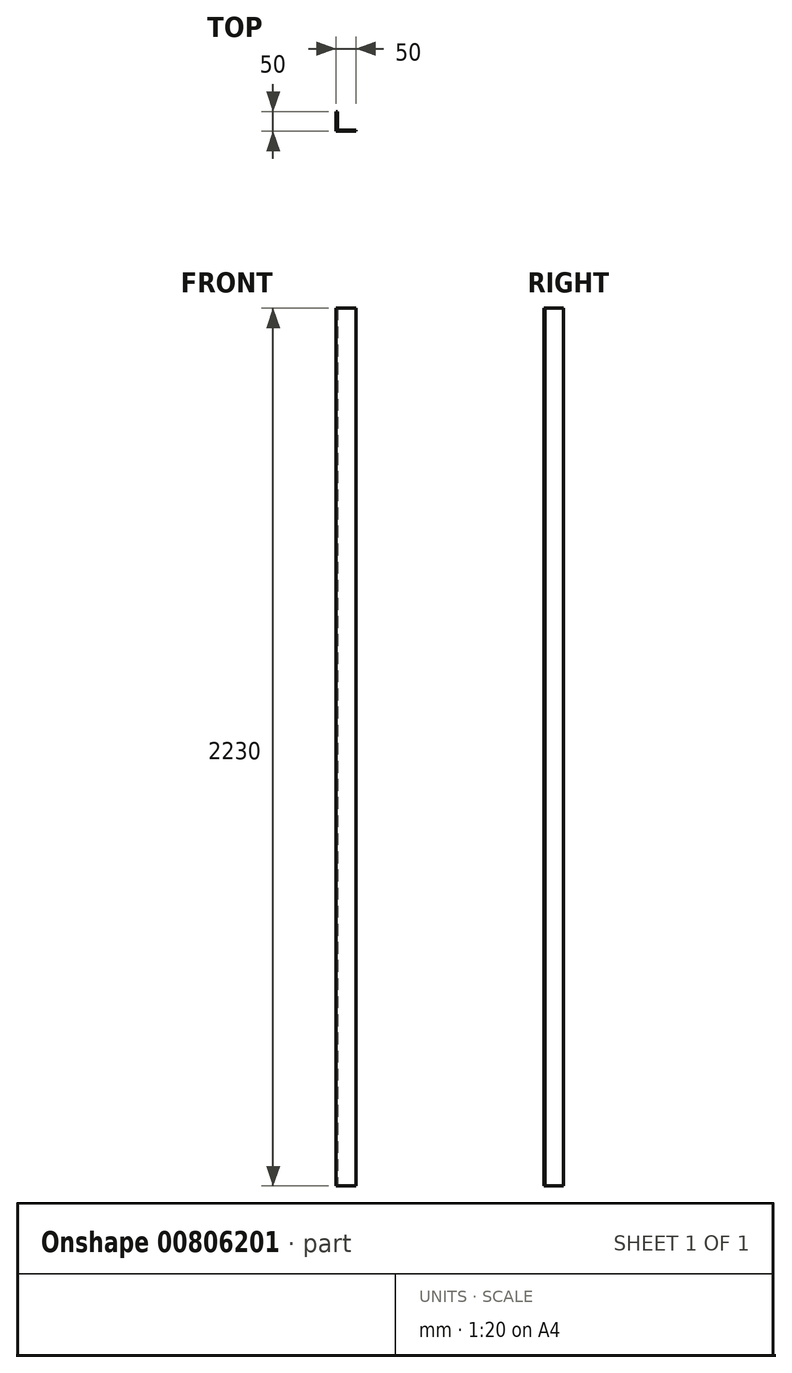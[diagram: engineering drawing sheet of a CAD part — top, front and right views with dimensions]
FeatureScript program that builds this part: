
annotation { "Feature Type Name" : "Feature", "Feature Type Description" : "" }
export const myFeature = defineFeature(function(context is Context, id is Id, definition is map)
    precondition{}
    {
        {
            var Q0;
            Q0=qCreatedBy(makeId("Top.planeOp"),FACE);
            var sketch = newSketch(context, id + "F0", { "sketchPlane" : qUnion([Q0])});
            skLineSegment(sketch, "E0", {"start": v(0, 0) * mm, "end": v(50, 0) * mm});
            skLineSegment(sketch, "E1", {"start": v(0, 0) * mm, "end": v(0, 50) * mm});
            skLineSegment(sketch, "E2.0", {"start": v(3, 3) * mm, "end": v(50, 3) * mm});
            skLineSegment(sketch, "E2.1", {"start": v(3, 3) * mm, "end": v(3, 50) * mm});
            skLineSegment(sketch, "E3", {"start": v(50, 0) * mm, "end": v(50, 3) * mm});
            skLineSegment(sketch, "E4", {"start": v(0, 50) * mm, "end": v(3, 50) * mm});
            skSolve(sketch);
        }
        {
            var Q0;
            Q0=makeQuery(id+"F0.imprint","IMPRINT",FACE,{"disambiguationData":[TD([[makeQuery(id+"F0.imprint","IMPRINT",EDGE,{"derivedFrom":sQuery(id+"F0.wireOp",EDGE,"E0")}),1.0]])]});
            extrude(context, id + "F1", {"entities" : qUnion([Q0]), "depth" : 2230 * mm, "offsetDistance" : 25 * mm});
        }
    });
